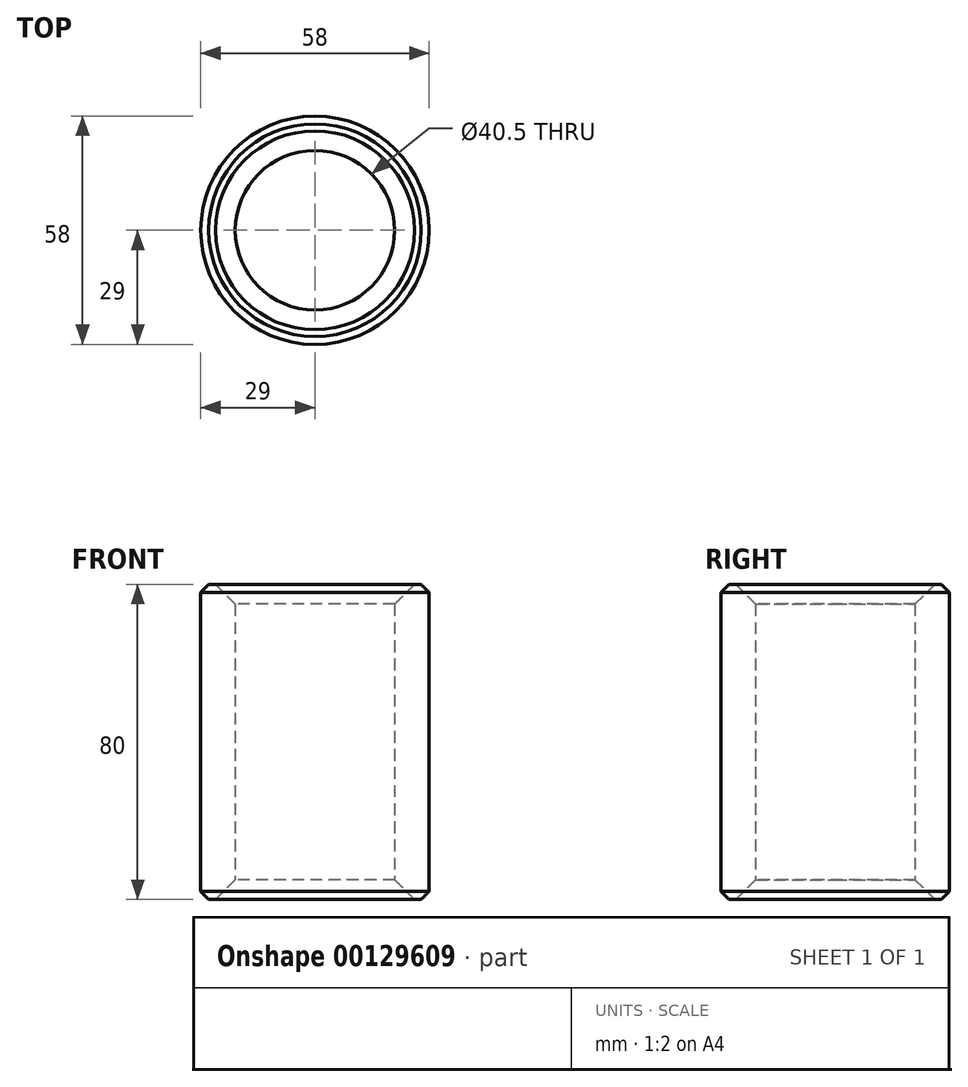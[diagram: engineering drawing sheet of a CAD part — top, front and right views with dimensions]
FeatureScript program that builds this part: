
annotation { "Feature Type Name" : "Feature", "Feature Type Description" : "" }
export const myFeature = defineFeature(function(context is Context, id is Id, definition is map)
    precondition{}
    {
        {
            var Q0;
            Q0=qCreatedBy(makeId("Top.planeOp"),FACE);
            var sketch = newSketch(context, id + "F0", { "sketchPlane" : qUnion([Q0])});
            skCircle(sketch, "E0", {"center": v(0, 0) * mm, "radius": 29 * mm});
            skCircle(sketch, "E1", {"center": v(0, 0) * mm, "radius": 20.25 * mm});
            skSolve(sketch);
        }
        {
            var Q0;
            Q0=qSketchRegion(id+"F0",true);
            extrude(context, id + "F1", {"entities" : qUnion([Q0]), "endBound" : BoundingType.SYMMETRIC, "depth" : 80 * mm});
        }
        {
            var Q0;
            Q0=makeQuery(id+"F1.opExtrude","CAP_EDGE",EDGE,{"disambiguationData":[OSD([sQuery(id+"F0.wireOp",EDGE,"E1")])],"isStart":false});
            chamfer(context, id + "F2", {"entities" : qUnion([Q0]), "width" : 5 * mm, "tangentPropagation" : true});
        }
        {
            var Q0;
            Q0=makeQuery(id+"F1.opExtrude","CAP_EDGE",EDGE,{"disambiguationData":[OSD([sQuery(id+"F0.wireOp",EDGE,"E0")])],"isStart":true});
            chamfer(context, id + "F3", {"entities" : qUnion([Q0]), "width" : 2 * mm, "tangentPropagation" : true});
        }
        {
            var Q0;
            Q0=makeQuery(id+"F1.opExtrude","CAP_EDGE",EDGE,{"disambiguationData":[OSD([sQuery(id+"F0.wireOp",EDGE,"E0")])],"isStart":false});
            chamfer(context, id + "F4", {"entities" : qUnion([Q0]), "width" : 2 * mm, "tangentPropagation" : true});
        }
        {
            var Q0;
            Q0=makeQuery(id+"F1.opExtrude","CAP_EDGE",EDGE,{"disambiguationData":[OSD([sQuery(id+"F0.wireOp",EDGE,"E1")])],"isStart":true});
            chamfer(context, id + "F5", {"entities" : qUnion([Q0]), "width" : 5 * mm, "tangentPropagation" : true});
        }
    });
